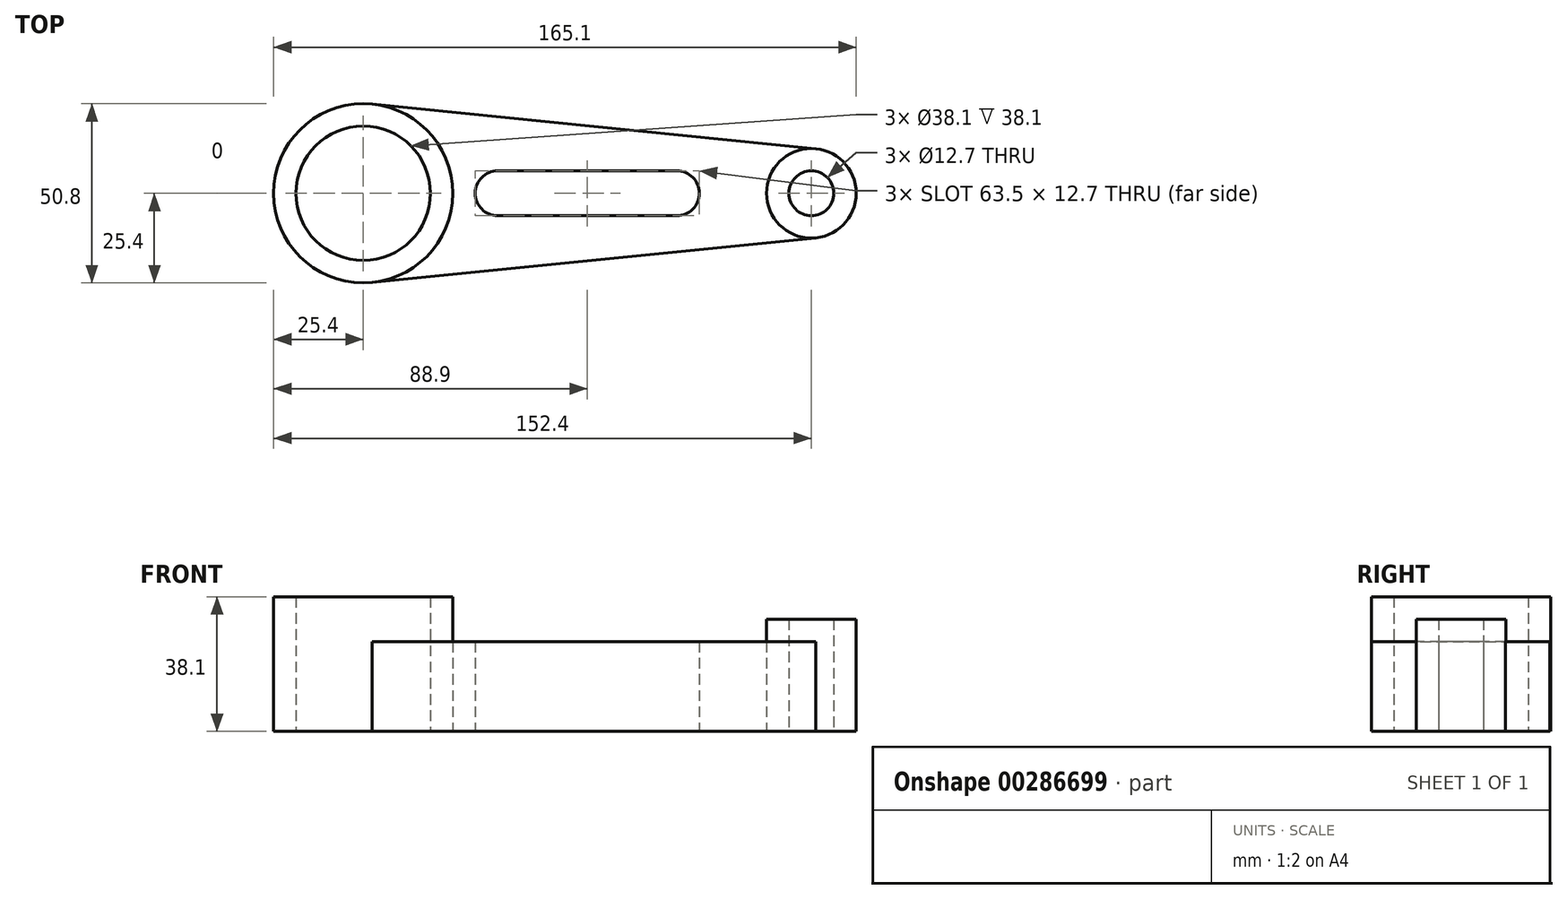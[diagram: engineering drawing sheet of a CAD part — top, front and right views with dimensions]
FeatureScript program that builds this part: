
annotation { "Feature Type Name" : "Feature", "Feature Type Description" : "" }
export const myFeature = defineFeature(function(context is Context, id is Id, definition is map)
    precondition{}
    {
        {
            var Q0;
            Q0=qCreatedBy(makeId("Top.planeOp"),FACE);
            var sketch = newSketch(context, id + "F0", { "sketchPlane" : qUnion([Q0])});
            skLineSegment(sketch, "E0", {"start": v(0, 6.35) * mm, "end": v(50.8, 6.35) * mm});
            skLineSegment(sketch, "E1", {"start": v(0, -6.35) * mm, "end": v(50.8, -6.35) * mm});
            skCircle(sketch, "E2", {"center": v(88.9, 0) * mm, "radius": 6.35 * mm});
            skCircle(sketch, "E3", {"center": v(88.9, 0) * mm, "radius": 12.7 * mm});
            skCircle(sketch, "E4", {"center": v(-38.1, 0) * mm, "radius": 19.05 * mm});
            skPoint(sketch, "E4.centerSnap0", {"position": v(-6.35, 0) * mm});
            skCircle(sketch, "E5", {"center": v(-38.1, 0) * mm, "radius": 25.4 * mm});
            skArc(sketch, "E6", {"start": v(0, 6.35) * mm, "mid": v(-6.35, 0) * mm, "end": v(0, -6.35) * mm});
            skPoint(sketch, "E7.center.orphan", {"position": v(50.8, 0) * mm});
            skArc(sketch, "E8", {"start": v(50.69, -6.35) * mm, "mid": v(57.15, -0.06) * mm, "end": v(50.8, 6.35) * mm});
            skLineSegment(sketch, "E9", {"start": v(-38.65, -25.58) * mm, "end": v(90.17, -12.64) * mm});
            skLineSegment(sketch, "E10", {"start": v(-35.56, 25.27) * mm, "end": v(90.17, 12.64) * mm});
            skSolve(sketch);
        }
        {
            var Q0;
            Q0=makeQuery(id+"F0.imprint","IMPRINT",FACE,{"disambiguationData":[TD([[makeQuery(id+"F0.imprint","IMPRINT",EDGE,{"derivedFrom":sQuery(id+"F0.wireOp",EDGE,"E4")}),-1.0]])]});
            extrude(context, id + "F1", {"entities" : qUnion([Q0]), "depth" : 38.1 * mm});
        }
        {
            var Q0;
            Q0=makeQuery(id+"F0.imprint","IMPRINT",FACE,{"disambiguationData":[TD([[makeQuery(id+"F0.imprint","IMPRINT",EDGE,{"derivedFrom":sQuery(id+"F0.wireOp",EDGE,"E2")}),-1.0]])]});
            extrude(context, id + "F2", {"entities" : qUnion([Q0]), "depth" : 31.75 * mm});
        }
        {
            var Q0;
            {var subQ7=sQuery(id+"F0.wireOp",EDGE,"E0");Q0=makeQuery(id+"F0.imprint","IMPRINT",FACE,{"disambiguationData":[TD([[makeQuery(id+"F0.imprint","IMPRINT",EDGE,{"derivedFrom":subQ7}),1.0]])]});}
            extrude(context, id + "F3", {"entities" : qUnion([Q0]), "depth" : 25.4 * mm});
        }
    });
